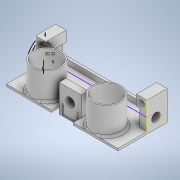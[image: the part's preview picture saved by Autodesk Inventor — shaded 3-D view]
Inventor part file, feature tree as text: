
AUTODESK INVENTOR PART (.ipt)
format: ipt  version: 2020 (Build 240168000, 168)  size: 433,152 bytes
history: native  units: mm
features: sketch x29, extrude x20, fillet x4
ambient origin geometry x8: Origin, YZ Plane, XZ Plane, XY Plane, X Axis, Y Axis, Z Axis, Center Point
bodies: Solid1 (feature_tree)
feature tree (53):
  sketch  "Sketch1"  dims[d3=25.4mm d4=25.4mm]
  extrude  "Extrusion1"  Depth=25.4mm
  extrude  "Extrusion2"  Depth=10.0mm TaperAngle=0.0deg
  extrude  "Extrusion3"  Depth=15.0mm
  sketch  "Sketch6"  dims[d14=14.85mm d15=0.0mm d16=20.32mm]
  extrude  "Extrusion4"  Depth=25.4mm TaperAngle=0.0deg
  sketch  "Sketch8"  dims[d19=3.25mm d20=150.0mm d21=10.0mm d22=0.0mm d23=0.0mm]
  extrude  "Extrusion5"  Depth=20.32mm
  extrude  "Extrusion6"  Depth=2.0mm
  sketch  "Sketch11"  dims[d29=25.4mm d30=0.0mm d31=18.0mm]
  extrude  "Extrusion7"  Depth=10.0mm TaperAngle=0.0deg
  extrude  "Extrusion8"  Depth=10.0mm
  extrude  "Extrusion9"  Depth=8.0mm
  sketch  "Sketch14"  dims[d39=31.75mm d40=20.0mm d41=0.0mm]
  sketch  "Sketch15"  dims[d42=25.0mm d43=10.0mm d44=0.0mm]
  sketch  "Sketch16"  dims[d45=31.75mm d46=10.0mm d47=0.0mm d48=12.7mm]
  extrude  "Extrusion10"  Depth=18.0mm
  extrude  "Extrusion11"  Depth=7.4mm
  sketch  "Sketch19"  dims[d60=1.5875mm d61=6.35mm d62=50.8mm]
  sketch  "Sketch20"  dims[d63=8.0mm d64=20.0mm d65=0.0mm]
  extrude  "Extrusion12"  Depth=14.9mm TaperAngle=0.0deg
  extrude  "Extrusion13"  Depth=20.0mm TaperAngle=0.0deg
  sketch  "Sketch23"  dims[d75=3.25mm d76=0.0mm]
  sketch  "Sketch24"  dims[d78=38.0mm]
  extrude  "Extrusion14"  Depth=10.0mm TaperAngle=0.0deg
  extrude  "Extrusion15"  Depth=10.0mm TaperAngle=0.0deg
  fillet  "Fillet1"  Radius=12.7mm
  sketch  "Sketch26"  dims[d81=3.0mm]
  extrude  "Extrusion16"  Depth=10.0mm
  extrude  "Extrusion17"  Depth=1.5875mm
  extrude  "Extrusion18"  Depth=6.35mm
  fillet  "Fillet2"  Radius=50.8mm
  extrude  "Extrusion19"  Depth=20.0mm TaperAngle=0.0deg
  extrude  "Extrusion20"  Depth=9.0mm
  fillet  "Fillet3"  Radius=41.5mm
  fillet  "Fillet4"  Radius=0.5mm
  sketch  "Sketch2"  dims[d5=12.7mm d6=10.0mm d7=0.0mm]
  sketch  "Sketch3"  dims[d8=15.0mm d9=15.0mm]
  sketch  "Sketch4"  dims[d10=8.0mm d11=25.4mm d12=0.0mm]
  sketch  "Sketch7"  dims[d17=41.275mm d18=2.0mm]
  sketch  "Sketch9"  dims[d24=10.0mm d25=0.0mm d26=15.0mm]
  sketch  "Sketch10"  dims[d27=15.0mm d28=8.0mm]
  sketch  "Sketch12"  dims[d32=25.4mm d33=0.0mm d34=7.4mm]
  sketch  "Sketch13"  dims[d35=14.9mm d36=0.0mm d37=14.9mm d38=0.0mm]
  sketch  "Sketch17"  dims[d49=10.0mm d50=0.0mm d51=21.0mm]
  sketch  "Sketch18"  dims[d58=1.5875mm d59=1.5875mm]
  sketch  "Sketch21"  dims[d66=15.0mm d67=0.0mm d68=9.0mm d70=41.5mm d71=0.5mm d72=0.0mm]
  sketch  "Sketch22"  dims[d74=41.5mm]
  sketch  "Sketch25"  dims[d79=39.0mm d80=0.0mm]
  sketch  "Sketch27"  dims[d82=3.5mm d83=0.0mm]
  sketch  "Sketch28"  dims[d84=2.25mm]
  sketch  "Sketch29"  dims[d85=2.25mm]
  sketch  "Sketch30"  dims[d86=3.5mm d87=0.0mm d88=1.1mm d89=1.1mm d73=0.5mm]
